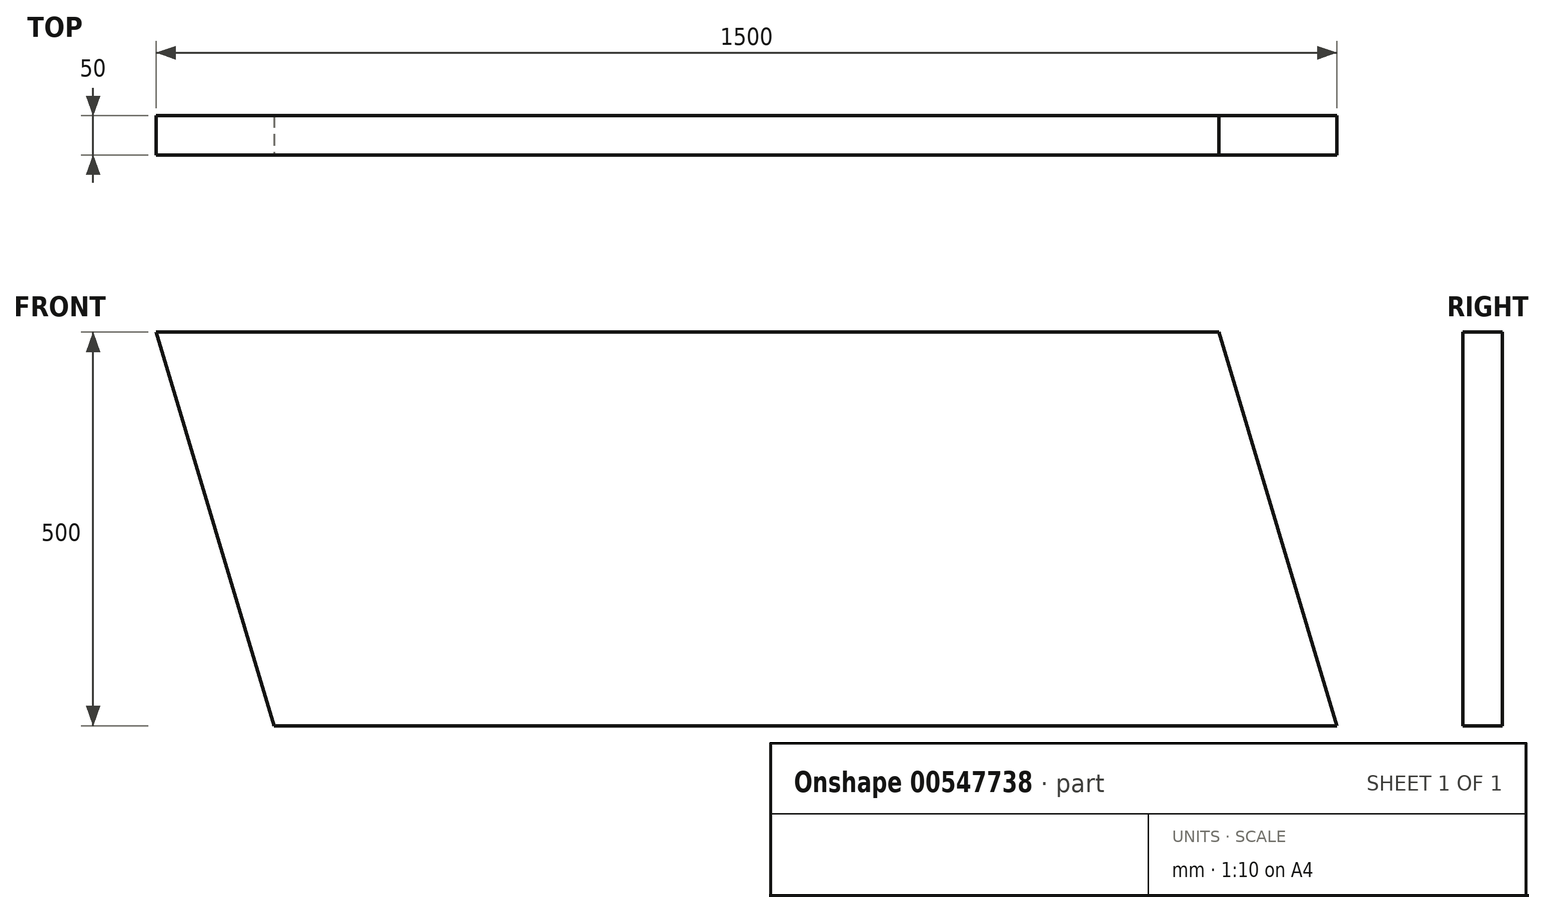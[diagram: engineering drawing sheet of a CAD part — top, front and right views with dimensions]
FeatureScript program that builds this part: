
annotation { "Feature Type Name" : "Feature", "Feature Type Description" : "" }
export const myFeature = defineFeature(function(context is Context, id is Id, definition is map)
    precondition{}
    {
        {
            var Q0;
            Q0=qCreatedBy(makeId("Top.planeOp"),FACE);
            var sketch = newSketch(context, id + "F0", { "sketchPlane" : qUnion([Q0])});
            skLineSegment(sketch, "E0.bottom", {"start": v(750, 25) * mm, "end": v(-750, 25) * mm});
            skLineSegment(sketch, "E0.top", {"start": v(750, -25) * mm, "end": v(-750, -25) * mm});
            skLineSegment(sketch, "E0.left", {"start": v(750, 25) * mm, "end": v(750, -25) * mm});
            skLineSegment(sketch, "E0.right", {"start": v(-750, 25) * mm, "end": v(-750, -25) * mm});
            skPoint(sketch, "E0.middle", {"position": v(0, 0) * mm});
            skSolve(sketch);
        }
        {
            var Q0;
            Q0=qSketchRegion(id+"F0",true);
            extrude(context, id + "F1", {"entities" : qUnion([Q0]), "endBound" : BoundingType.SYMMETRIC, "depth" : 500 * mm, "offsetDistance" : 25 * mm});
        }
        {
            var Q0;
            Q0=makeQuery(id+"F1.opExtrude","SWEPT_FACE",FACE,{"disambiguationData":[OSD([sQuery(id+"F0.wireOp",EDGE,"E0.top")])]});
            var sketch = newSketch(context, id + "F2", { "sketchPlane" : qUnion([Q0])});
            skLineSegment(sketch, "E1", {"start": v(-750, 250) * mm, "end": v(-600, -250) * mm});
            skLineSegment(sketch, "E2", {"start": v(750, -250) * mm, "end": v(600, 250) * mm});
            skLineSegment(sketch, "E3", {"start": v(-750, 250) * mm, "end": v(-750, -250) * mm});
            skLineSegment(sketch, "E4", {"start": v(-750, -250) * mm, "end": v(-600, -250) * mm});
            skLineSegment(sketch, "E5", {"start": v(750, -250) * mm, "end": v(750, 250) * mm});
            skLineSegment(sketch, "E6", {"start": v(750, 250) * mm, "end": v(600, 250) * mm});
            skSolve(sketch);
        }
        {
            var Q0;
            Q0 = qSketchRegion(id + "F2", true);
            extrude(context, id + "F3", {"entities" : qUnion([Q0]), "operationType" : NewBodyOperationType.REMOVE, "endBound" : BoundingType.UP_TO_NEXT, "oppositeDirection" : true, "depth" : 25 * mm, "offsetDistance" : 25 * mm});
        }
    });
